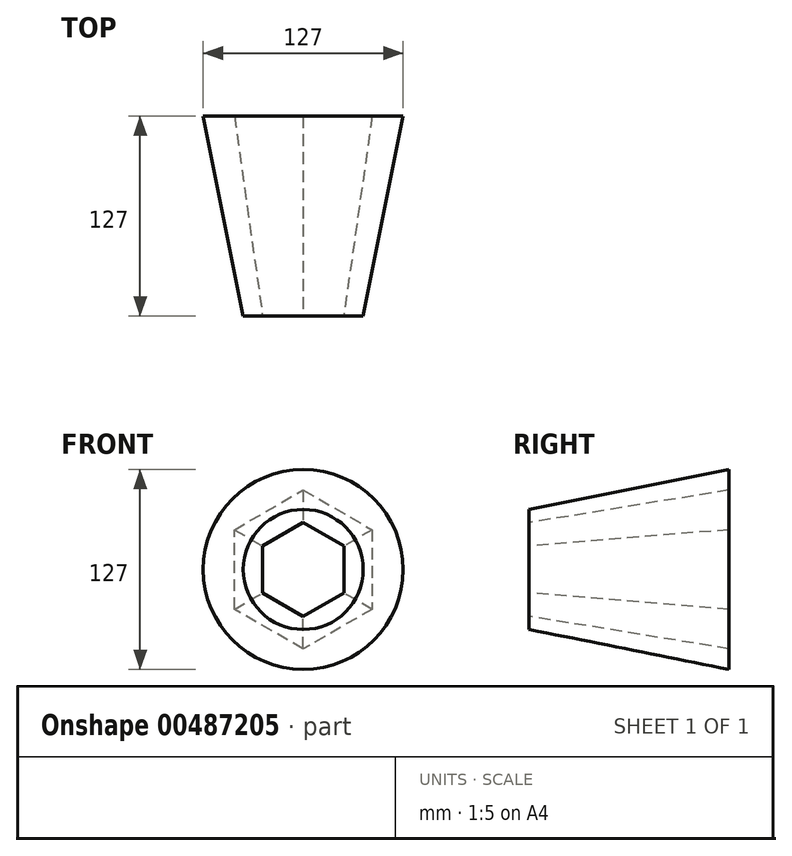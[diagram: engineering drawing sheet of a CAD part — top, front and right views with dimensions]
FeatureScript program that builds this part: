
annotation { "Feature Type Name" : "Feature", "Feature Type Description" : "" }
export const myFeature = defineFeature(function(context is Context, id is Id, definition is map)
    precondition{}
    {
        {
            var Q0;
            Q0=qCreatedBy(makeId("Front.planeOp"),FACE);
            cPlane(context, id + "F0", {"entities" : qUnion([Q0]), "cplaneType" : CPlaneType.OFFSET, "offset" : 127 * mm, "width" : 152.4 * mm, "height" : 152.4 * mm});
        }
        {
            var Q0;
            Q0=qCreatedBy(makeId("Front.planeOp"),FACE);
            var sketch = newSketch(context, id + "F1", { "sketchPlane" : qUnion([Q0])});
            skCircle(sketch, "E0", {"center": v(0, 0) * mm, "radius": 63.5 * mm});
            skSolve(sketch);
        }
        {
            var Q0;
            Q0=qCreatedBy(id+"F0.planeOp",FACE);
            var sketch = newSketch(context, id + "F2", { "sketchPlane" : qUnion([Q0])});
            skCircle(sketch, "E1", {"center": v(0, 0) * mm, "radius": 38.1 * mm});
            skSolve(sketch);
        }
        {
            var Q0;
            Q0=makeQuery(id+"F1.imprint","IMPRINT",FACE,{"disambiguationData":[TD([[makeQuery(id+"F1.imprint","IMPRINT",EDGE,{"derivedFrom":sQuery(id+"F1.wireOp",EDGE,"E0")}),1.0]])]});
            var Q1;
            Q1=makeQuery(id+"F2.imprint","IMPRINT",FACE,{"disambiguationData":[TD([[makeQuery(id+"F2.imprint","IMPRINT",EDGE,{"derivedFrom":sQuery(id+"F2.wireOp",EDGE,"E1")}),1.0]])]});
            loft(context, id + "F3", {"sheetProfilesArray" : [{ "sheetProfileEntities" : qUnion([Q0]) }, { "sheetProfileEntities" : qUnion([Q1]) }]});
        }
        {
            var Q0;
            Q0=qCreatedBy(id+"F0.planeOp",FACE);
            var sketch = newSketch(context, id + "F4", { "sketchPlane" : qUnion([Q0])});
            skCircle(sketch, "E2.cCircle", {"center": v(0, 0) * mm, "radius": 25.78 * mm, "construction": true});
            skLineSegment(sketch, "E2.0", {"start": v(25.78, 14.89) * mm, "end": v(25.78, -14.89) * mm});
            skLineSegment(sketch, "E2.1", {"start": v(25.78, -14.89) * mm, "end": v(0, -29.77) * mm});
            skLineSegment(sketch, "E2.2", {"start": v(0, -29.77) * mm, "end": v(-25.78, -14.89) * mm});
            skLineSegment(sketch, "E2.3", {"start": v(-25.78, -14.89) * mm, "end": v(-25.78, 14.89) * mm});
            skLineSegment(sketch, "E2.4", {"start": v(-25.78, 14.89) * mm, "end": v(0, 29.77) * mm});
            skLineSegment(sketch, "E2.5", {"start": v(0, 29.77) * mm, "end": v(25.78, 14.89) * mm});
            skPoint(sketch, "E2.0.midPoint", {"position": v(25.78, 0) * mm});
            skSolve(sketch);
        }
        {
            var Q0;
            Q0=qCreatedBy(makeId("Front.planeOp"),FACE);
            var sketch = newSketch(context, id + "F5", { "sketchPlane" : qUnion([Q0])});
            skCircle(sketch, "E3.cCircle", {"center": v(0, 0) * mm, "radius": 43.7 * mm, "construction": true});
            skLineSegment(sketch, "E3.0", {"start": v(43.7, 25.23) * mm, "end": v(43.7, -25.23) * mm});
            skLineSegment(sketch, "E3.1", {"start": v(43.7, -25.23) * mm, "end": v(0, -50.46) * mm});
            skLineSegment(sketch, "E3.2", {"start": v(0, -50.46) * mm, "end": v(-43.7, -25.23) * mm});
            skLineSegment(sketch, "E3.3", {"start": v(-43.7, -25.23) * mm, "end": v(-43.7, 25.23) * mm});
            skLineSegment(sketch, "E3.4", {"start": v(-43.7, 25.23) * mm, "end": v(0, 50.46) * mm});
            skLineSegment(sketch, "E3.5", {"start": v(0, 50.46) * mm, "end": v(43.7, 25.23) * mm});
            skPoint(sketch, "E3.0.midPoint", {"position": v(43.7, 0) * mm});
            skSolve(sketch);
        }
        {
            var Q1;
            Q1=makeQuery(id+"F5.imprint","IMPRINT",FACE,{"disambiguationData":[TD([[makeQuery(id+"F5.imprint","IMPRINT",EDGE,{"derivedFrom":sQuery(id+"F5.wireOp",EDGE,"E3.0")}),-1.0]])]});
            var Q2;
            Q2=makeQuery(id+"F4.imprint","IMPRINT",FACE,{"disambiguationData":[TD([[makeQuery(id+"F4.imprint","IMPRINT",EDGE,{"derivedFrom":sQuery(id+"F4.wireOp",EDGE,"E2.0")}),-1.0]])]});
            loft(context, id + "F6", {"operationType" : NewBodyOperationType.REMOVE, "sheetProfilesArray" : [{ "sheetProfileEntities" : qUnion([Q1]) }, { "sheetProfileEntities" : qUnion([Q2]) }]});
        }
    });
